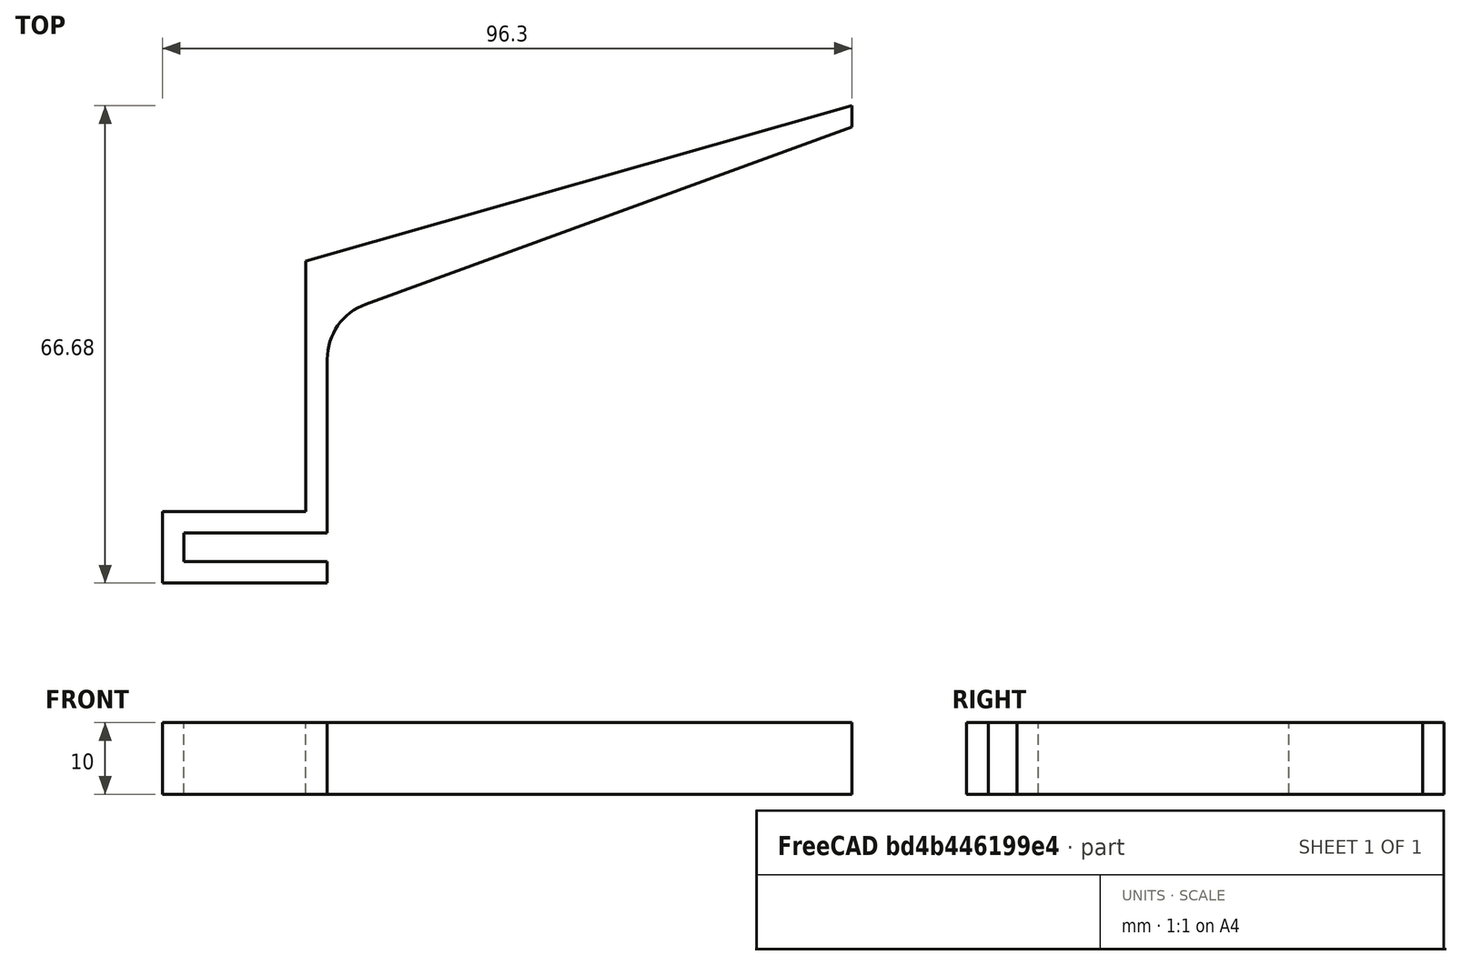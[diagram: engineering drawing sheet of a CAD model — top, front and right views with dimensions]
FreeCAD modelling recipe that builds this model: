
FCSTD DOCUMENT  (FreeCAD 0.22R38261 (Git))
Label: профиль лодки
License: All rights reserved
LicenseURL: https://en.wikipedia.org/wiki/All_rights_reserved
objects: Sketcher::SketchObject×1, PartDesign::Pad×1, PartDesign::Body×1
note: 5 computed .brp shape members not serialized (recipe doc carries the construction recipe); baked Part::Feature solids carry a one-line shape summary decoded from their .brp

FEATURE [Sketcher::SketchObject] Sketch
  AttachmentSupport = -> [XY_Plane]
  FullyConstrained = true
  MapMode = 5
  sketch-geometry (15):
    g0: LineSegment StartX=0 StartY=-4 StartZ=0 EndX=20 EndY=-4 EndZ=0
    g1: GeomPoint X=0 Y=-4 Z=0
    g2: LineSegment StartX=20 StartY=-4 StartZ=0 EndX=20 EndY=-7 EndZ=0
    g3: LineSegment StartX=20 StartY=-7 StartZ=0 EndX=-3 EndY=-7 EndZ=0
    g4: LineSegment StartX=-3 StartY=-7 StartZ=0 EndX=-3 EndY=3 EndZ=0
    g5: LineSegment StartX=-3 StartY=3 StartZ=0 EndX=17 EndY=3 EndZ=0
    g6: LineSegment StartX=20 StartY=0 StartZ=0 EndX=20 EndY=24.2687 EndZ=0
    g7: LineSegment StartX=25.3856 StartY=31.9602 StartZ=0 EndX=93.296 EndY=56.6776 EndZ=0
    g8: ArcOfCircle CenterX=28.1851 CenterY=24.2687 CenterZ=0 NormalX=0 NormalY=0 NormalZ=1 AngleXU=0 Radius=8.18511 StartAngle=1.91986 EndAngle=3.14159
    g9: GeomPoint X=20 Y=30 Z=0
    g10: LineSegment StartX=17 StartY=3 StartZ=0 EndX=17 EndY=38 EndZ=0
    g11: LineSegment StartX=93.296 StartY=56.6776 StartZ=0 EndX=93.296 EndY=59.6776 EndZ=0
    g12: LineSegment StartX=17 StartY=38 StartZ=0 EndX=93.296 EndY=59.6776 EndZ=0
    g13: LineSegment StartX=0 StartY=-4 StartZ=0 EndX=0 EndY=0 EndZ=0
    g14: LineSegment StartX=0 StartY=0 StartZ=0 EndX=20 EndY=0 EndZ=0
  constraints (41):
    c: PointOnObject(g1,g-2)
    c: Distance(g-1,g1) = 4
    c: Horizontal(g0)
    c: PointOnObject(g1,g0)
    c: Coincident(g2,g0)
    c: Vertical(g2)
    c: Coincident(g3,g2)
    c: Horizontal(g3)
    c: Coincident(g4,g3)
    c: Vertical(g4)
    c: Horizontal(g5)
    c: Distance(g2) = 3
    c: Coincident(g4,g5)
    c: Vertical(g6)
    c: DistanceY(g6,g9) = 30
    c: Distance(g7,g9) = 78
    c: PointOnObject(g9,g6)
    c: PointOnObject(g9,g7)
    c: Tangent(g6,g8) = 1.5708
    c: Tangent(g7,g8) = 1.5708
    c: Angle(g6,g7) = 1.91986
    c: Coincident(g10,g5)
    c: Vertical(g10)
    c: Coincident(g11,g7)
    c: Vertical(g11)
    c: DistanceY(g11,g11) = 3
    c: Coincident(g12,g10)
    c: Coincident(g12,g11)
    c: DistanceX(g5,g6) = 3
    c: Coincident(g13,g0)
    c: Coincident(g13,g-1)
    c: Vertical(g13)
    c: Coincident(g14,g-1)
    c: Coincident(g14,g6)
    c: Horizontal(g14)
    c: DistanceX(g14,g14) = 20
    c: DistanceX(g0,g0) = 20
    c: DistanceX(g3,g1) = 3
    c: DistanceY(g13,g4) = 3
    c: DistanceY(g10,g10) = 35
    c: Distance(g8) = 10
FEATURE [PartDesign::Pad] Pad
  Direction = (0,0,1)
  Length = 10
  Length2 = 10
  Profile = -> Sketch
  ReferenceAxis = -> Sketch [N_Axis]
  Suppressed = false
  Type = 0
FEATURE [PartDesign::Body] Body
  AllowCompound = false
  Group = -> [Sketch,Pad]
  Origin = -> Origin
  Tip = -> Pad
